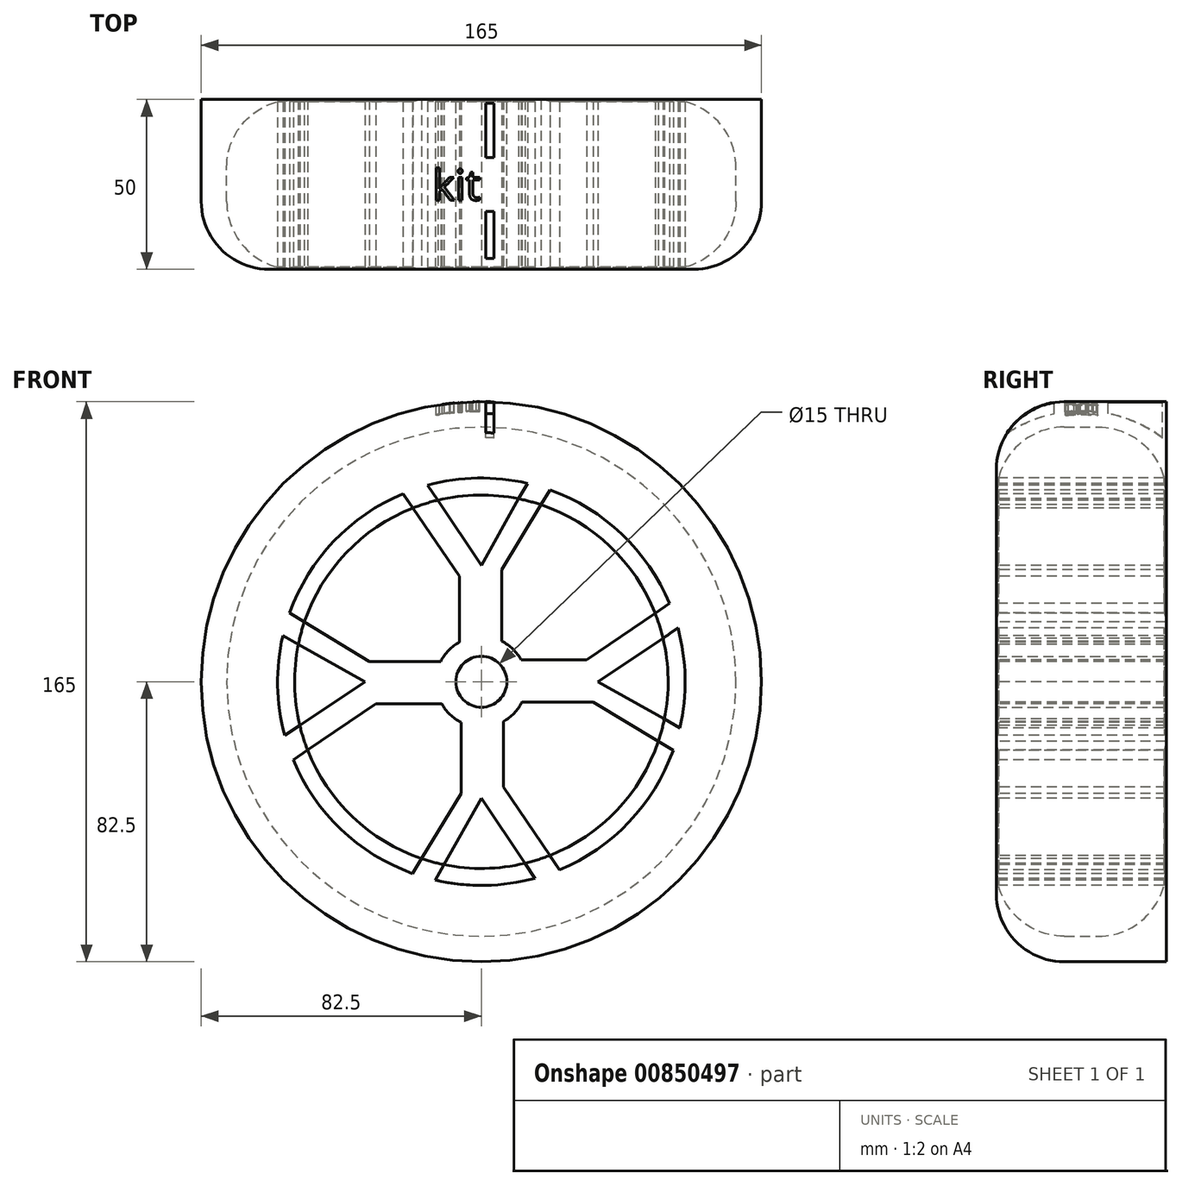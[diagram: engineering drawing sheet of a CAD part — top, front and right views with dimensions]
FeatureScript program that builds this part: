
annotation { "Feature Type Name" : "Feature", "Feature Type Description" : "" }
export const myFeature = defineFeature(function(context is Context, id is Id, definition is map)
    precondition{}
    {
        {
            var Q0;
            Q0=qCreatedBy(makeId("Front.planeOp"),FACE);
            var sketch = newSketch(context, id + "F0", { "sketchPlane" : qUnion([Q0])});
            skCircle(sketch, "E0", {"center": v(0, 0) * mm, "radius": 75 * mm});
            skCircle(sketch, "E1", {"center": v(0, 0) * mm, "radius": 7.5 * mm});
            skSolve(sketch);
        }
        {
            var Q0;
            Q0=makeQuery(id+"F0.imprint","IMPRINT",FACE,{"disambiguationData":[TD([[makeQuery(id+"F0.imprint","IMPRINT",EDGE,{"derivedFrom":sQuery(id+"F0.wireOp",EDGE,"E0")}),1.0]])]});
            var Q1;
            Q1 = qSketchRegion(id + "F2", true);
            extrude(context, id + "F1", {"entities" : qUnion([Q0, Q1]), "depth" : 25 * mm, "offsetDistance" : 25 * mm});
        }
        {
            var Q0;
            Q0=makeQuery(id+"F1.opExtrude","CAP_FACE",FACE,{"disambiguationData":[OSD([sQuery(id+"F0.wireOp",EDGE,"E0")])],"isStart":false});
            var sketch = newSketch(context, id + "F2", { "sketchPlane" : qUnion([Q0])});
            skPoint(sketch, "E2.center", {"position": v(0, 0) * mm});
            skCircle(sketch, "E3", {"center": v(0, 0) * mm, "radius": 60 * mm});
            skLineSegment(sketch, "E4", {"start": v(-13.56, -58.45) * mm, "end": v(0, -34.29) * mm});
            skLineSegment(sketch, "E5", {"start": v(0, -34.29) * mm, "end": v(15.8, -57.88) * mm});
            skLineSegment(sketch, "E6", {"start": v(6.45, -43.93) * mm, "end": v(6.45, 0) * mm});
            skLineSegment(sketch, "E7", {"start": v(-5.99, -44.96) * mm, "end": v(-5.99, 0) * mm});
            skCircle(sketch, "E8", {"center": v(0, 0) * mm, "radius": 10.6 * mm});
            skLineSegment(sketch, "E9", {"start": v(-20.24, -56.48) * mm, "end": v(-5.99, -32.95) * mm});
            skLineSegment(sketch, "E10", {"start": v(6.45, -31.06) * mm, "end": v(23.04, -55.4) * mm});
            skLineSegment(sketch, "E11.1.0", {"start": v(56.48, -20.24) * mm, "end": v(32.95, -5.99) * mm});
            skLineSegment(sketch, "E11.1.1", {"start": v(58.45, -13.56) * mm, "end": v(34.29, 0) * mm});
            skLineSegment(sketch, "E11.1.2", {"start": v(44.96, -5.99) * mm, "end": v(0, -5.99) * mm});
            skLineSegment(sketch, "E11.1.3", {"start": v(43.93, 6.45) * mm, "end": v(0, 6.45) * mm});
            skLineSegment(sketch, "E11.1.4", {"start": v(31.06, 6.45) * mm, "end": v(55.4, 23.04) * mm});
            skLineSegment(sketch, "E11.1.5", {"start": v(34.29, 0) * mm, "end": v(57.88, 15.8) * mm});
            skLineSegment(sketch, "E11.2.0", {"start": v(20.24, 56.48) * mm, "end": v(5.99, 32.95) * mm});
            skLineSegment(sketch, "E11.2.1", {"start": v(13.56, 58.45) * mm, "end": v(0, 34.29) * mm});
            skLineSegment(sketch, "E11.2.2", {"start": v(5.99, 44.96) * mm, "end": v(5.99, 0) * mm});
            skLineSegment(sketch, "E11.2.3", {"start": v(-6.45, 43.93) * mm, "end": v(-6.45, 0) * mm});
            skLineSegment(sketch, "E11.2.4", {"start": v(-6.45, 31.06) * mm, "end": v(-23.04, 55.4) * mm});
            skLineSegment(sketch, "E11.2.5", {"start": v(0, 34.29) * mm, "end": v(-15.8, 57.88) * mm});
            skLineSegment(sketch, "E11.3.0", {"start": v(-56.48, 20.24) * mm, "end": v(-32.95, 5.99) * mm});
            skLineSegment(sketch, "E11.3.1", {"start": v(-58.45, 13.56) * mm, "end": v(-34.29, 0) * mm});
            skLineSegment(sketch, "E11.3.2", {"start": v(-44.96, 5.99) * mm, "end": v(0, 5.99) * mm});
            skLineSegment(sketch, "E11.3.3", {"start": v(-43.93, -6.45) * mm, "end": v(0, -6.45) * mm});
            skLineSegment(sketch, "E11.3.4", {"start": v(-31.06, -6.45) * mm, "end": v(-55.4, -23.04) * mm});
            skLineSegment(sketch, "E11.3.5", {"start": v(-34.29, 0) * mm, "end": v(-57.88, -15.8) * mm});
            skLineSegment(sketch, "E12", {"start": v(49.36, -34.12) * mm, "end": v(29.65, -13.58) * mm});
            skLineSegment(sketch, "E13", {"start": v(29.65, -13.58) * mm, "end": v(12.4, -9.8) * mm});
            skLineSegment(sketch, "E14", {"start": v(12.4, -9.8) * mm, "end": v(14.53, -27.76) * mm});
            skLineSegment(sketch, "E15", {"start": v(14.53, -27.76) * mm, "end": v(35.64, -48.26) * mm});
            skLineSegment(sketch, "E16.1.0", {"start": v(34.12, 49.36) * mm, "end": v(13.58, 29.65) * mm});
            skLineSegment(sketch, "E16.1.1", {"start": v(13.58, 29.65) * mm, "end": v(9.8, 12.4) * mm});
            skLineSegment(sketch, "E16.1.2", {"start": v(9.8, 12.4) * mm, "end": v(27.76, 14.53) * mm});
            skLineSegment(sketch, "E16.1.3", {"start": v(27.76, 14.53) * mm, "end": v(48.26, 35.64) * mm});
            skLineSegment(sketch, "E16.2.0", {"start": v(-49.36, 34.12) * mm, "end": v(-29.65, 13.58) * mm});
            skLineSegment(sketch, "E16.2.1", {"start": v(-29.65, 13.58) * mm, "end": v(-12.4, 9.8) * mm});
            skLineSegment(sketch, "E16.2.2", {"start": v(-12.4, 9.8) * mm, "end": v(-14.53, 27.76) * mm});
            skLineSegment(sketch, "E16.2.3", {"start": v(-14.53, 27.76) * mm, "end": v(-35.64, 48.26) * mm});
            skLineSegment(sketch, "E16.3.0", {"start": v(-34.12, -49.36) * mm, "end": v(-13.58, -29.65) * mm});
            skLineSegment(sketch, "E16.3.1", {"start": v(-13.58, -29.65) * mm, "end": v(-9.8, -12.4) * mm});
            skLineSegment(sketch, "E16.3.2", {"start": v(-9.8, -12.4) * mm, "end": v(-27.76, -14.53) * mm});
            skLineSegment(sketch, "E16.3.3", {"start": v(-27.76, -14.53) * mm, "end": v(-48.26, -35.64) * mm});
            skCircle(sketch, "E17", {"center": v(0, 0) * mm, "radius": 13.37 * mm});
            skSolve(sketch);
        }
        {
            var Q0;
            Q0=makeQuery(id+"F1.opExtrude","CAP_EDGE",EDGE,{"disambiguationData":[OSD([sQuery(id+"F0.wireOp",EDGE,"E0")])],"isStart":false});
            fillet(context, id + "F3", {"entities" : qUnion([Q0]), "radius" : 20 * mm, "tangentPropagation" : true, "allowEdgeOverflow" : false});
        }
        {
            var Q0;
            Q0=makeQuery(id+"F1.opExtrude","SWEPT_BODY",BODY,{"disambiguationData":[OSD([sQuery(id+"F0.wireOp",EDGE,"E0")])]});
            var Q1;
            Q1=makeQuery(id+"F1.opExtrude","CAP_FACE",FACE,{"disambiguationData":[OSD([sQuery(id+"F0.wireOp",EDGE,"E0")])],"isStart":true});
            mirror(context, id + "F4", {"operationType" : NewBodyOperationType.ADD, "entities" : qUnion([Q0]), "mirrorPlane" : qUnion([Q1])});
        }
        {
            var Q0;
            Q0=makeQuery(id+"F1.opExtrude","CAP_FACE",FACE,{"disambiguationData":[OSD([sQuery(id+"F0.wireOp",EDGE,"E0"),sQuery(id+"F0.wireOp",EDGE,"E1")])],"isStart":false});
            var sketch = newSketch(context, id + "F5", { "sketchPlane" : qUnion([Q0])});
            skCircle(sketch, "E18", {"center": v(0, 0) * mm, "radius": 82.5 * mm});
            skCircle(sketch, "E19", {"center": v(0, 0) * mm, "radius": 75 * mm});
            skSolve(sketch);
        }
        {
            var Q0;
            Q0=makeQuery(id+"F5.imprint","IMPRINT",FACE,{"disambiguationData":[TD([[makeQuery(id+"F5.imprint","IMPRINT",EDGE,{"derivedFrom":sQuery(id+"F5.wireOp",EDGE,"E18")}),1.0]])]});
            var Q1;
            Q1=makeQuery(id+"F5.imprint","IMPRINT",FACE,{"disambiguationData":[TD([[makeQuery(id+"F5.imprint","IMPRINT",EDGE,{"derivedFrom":sQuery(id+"F5.wireOp",EDGE,"E19")}),1.0]])]});
            var Q2;
            Q2=makeQuery(id+"F4.opPattern","COPY",FACE,{"derivedFrom":makeQuery(id+"F1.opExtrude","CAP_FACE",FACE,{"disambiguationData":[OSD([sQuery(id+"F0.wireOp",EDGE,"E0"),sQuery(id+"F0.wireOp",EDGE,"E1")])],"isStart":false}),"instanceName":"1"});
            extrude(context, id + "F6", {"entities" : qUnion([Q0, Q1]), "endBound" : BoundingType.UP_TO_SURFACE, "oppositeDirection" : true, "depth" : 25 * mm, "endBoundEntityFace" : qUnion([Q2]), "offsetDistance" : 25 * mm});
        }
        {
            var Q0;
            Q0=makeQuery(id+"F6.opExtrude","CAP_EDGE",EDGE,{"disambiguationData":[OSD([sQuery(id+"F5.wireOp",EDGE,"E18")])],"isStart":true});
            var Q1;
            Q1=makeQuery(id+"F6.opExtrude","TWEAK_EDGE",EDGE,{"derivedFrom":[makeQuery(id+"F4.opPattern","COPY",FACE,{"derivedFrom":makeQuery(id+"F1.opExtrude","CAP_FACE",FACE,{"disambiguationData":[OSD([sQuery(id+"F0.wireOp",EDGE,"E0"),sQuery(id+"F0.wireOp",EDGE,"E1")])],"isStart":false}),"instanceName":"1"}),makeQuery(id+"F5.imprint","IMPRINT",EDGE,{"derivedFrom":sQuery(id+"F5.wireOp",EDGE,"E18")})]});
            fillet(context, id + "F7", {"entities" : qUnion([Q0, Q1]), "radius" : 20 * mm, "tangentPropagation" : true, "allowEdgeOverflow" : false});
        }
        {
            var Q0;
            Q0=qCreatedBy(makeId("Right.planeOp"),FACE);
            var sketch = newSketch(context, id + "F8", { "sketchPlane" : qUnion([Q0])});
            skArc(sketch, "E20", {"start": v(26.8, 69.52) * mm, "mid": v(1.15, 79.8) * mm, "end": v(-25.05, 71) * mm});
            skSolve(sketch);
        }
        {
            var Q0;
            Q0=sQuery(id+"F8.wireOp",EDGE,"E20");
            var Q1;
            Q1=sQuery(id+"F0.wireOp",EDGE,"E1");
            revolve(context, id + "F9", {"bodyType" : ToolBodyType.SURFACE, "surfaceOperationType" : NewSurfaceOperationType.NEW, "surfaceEntities" : qUnion([Q0]), "axis" : qUnion([Q1]), "revolveType" : RevolveType.FULL});
        }
        {
            var Q0;
            {var subQ1=sQuery(id+"F2.wireOp",EDGE,"E10");Q0=makeQuery(id+"F2.imprint","IMPRINT",FACE,{"disambiguationData":[TD([[makeQuery(id+"F2.imprint","IMPRINT",EDGE,{"derivedFrom":subQ1}),1.0]])]});}
            var Q1;
            {var subQ7=sQuery(id+"F2.wireOp",EDGE,"E11.1.4");Q1=makeQuery(id+"F2.imprint","IMPRINT",FACE,{"disambiguationData":[TD([[makeQuery(id+"F2.imprint","IMPRINT",EDGE,{"derivedFrom":subQ7}),1.0]])]});}
            var Q2;
            {var subQ0=sQuery(id+"F2.wireOp",EDGE,"E16.1.0");Q2=makeQuery(id+"F2.imprint","IMPRINT",FACE,{"disambiguationData":[TD([[makeQuery(id+"F2.imprint","IMPRINT",EDGE,{"derivedFrom":subQ0}),1.0]])]});}
            var Q3;
            {var subQ0=sQuery(id+"F2.wireOp",EDGE,"E12");Q3=makeQuery(id+"F2.imprint","IMPRINT",FACE,{"disambiguationData":[TD([[makeQuery(id+"F2.imprint","IMPRINT",EDGE,{"derivedFrom":subQ0}),1.0]])]});}
            var Q4;
            {var subQ0=sQuery(id+"F2.wireOp",EDGE,"E11.1.1");var subQ1=sQuery(id+"F2.wireOp",EDGE,"E3");var subQ2=makeQuery(id+"F2.imprint","INTERSECT",VERTEX,{"derivedFrom":[subQ1,subQ0]});Q4=makeQuery(id+"F2.imprint","IMPRINT",FACE,{"disambiguationData":[TD([[makeQuery(id+"F2.imprint","IMPRINT",EDGE,{"disambiguationData":[TD([[subQ2,-1.0]])],"derivedFrom":subQ1}),1.0]])]});}
            var Q5;
            {var subQ1=sQuery(id+"F2.wireOp",EDGE,"E11.2.1");var subQ4=sQuery(id+"F2.wireOp",EDGE,"E3");var subQ5=makeQuery(id+"F2.imprint","INTERSECT",VERTEX,{"derivedFrom":[subQ4,subQ1]});Q5=makeQuery(id+"F2.imprint","IMPRINT",FACE,{"disambiguationData":[TD([[makeQuery(id+"F2.imprint","IMPRINT",EDGE,{"disambiguationData":[TD([[subQ5,-1.0]])],"derivedFrom":subQ4}),1.0]])]});}
            var Q6;
            {var subQ0=sQuery(id+"F2.wireOp",EDGE,"E16.2.0");Q6=makeQuery(id+"F2.imprint","IMPRINT",FACE,{"disambiguationData":[TD([[makeQuery(id+"F2.imprint","IMPRINT",EDGE,{"derivedFrom":subQ0}),1.0]])]});}
            var Q7;
            {var subQ1=sQuery(id+"F2.wireOp",EDGE,"E11.2.4");Q7=makeQuery(id+"F2.imprint","IMPRINT",FACE,{"disambiguationData":[TD([[makeQuery(id+"F2.imprint","IMPRINT",EDGE,{"derivedFrom":subQ1}),1.0]])]});}
            var Q8;
            {var subQ0=sQuery(id+"F2.wireOp",EDGE,"E11.3.1");var subQ1=sQuery(id+"F2.wireOp",EDGE,"E3");var subQ2=makeQuery(id+"F2.imprint","INTERSECT",VERTEX,{"derivedFrom":[subQ1,subQ0]});Q8=makeQuery(id+"F2.imprint","IMPRINT",FACE,{"disambiguationData":[TD([[makeQuery(id+"F2.imprint","IMPRINT",EDGE,{"disambiguationData":[TD([[subQ2,-1.0]])],"derivedFrom":subQ1}),1.0]])]});}
            var Q9;
            {var subQ0=sQuery(id+"F2.wireOp",EDGE,"E16.3.0");Q9=makeQuery(id+"F2.imprint","IMPRINT",FACE,{"disambiguationData":[TD([[makeQuery(id+"F2.imprint","IMPRINT",EDGE,{"derivedFrom":subQ0}),1.0]])]});}
            var Q10;
            {var subQ0=sQuery(id+"F2.wireOp",EDGE,"E9");Q10=makeQuery(id+"F2.imprint","IMPRINT",FACE,{"disambiguationData":[TD([[makeQuery(id+"F2.imprint","IMPRINT",EDGE,{"derivedFrom":subQ0}),1.0]])]});}
            var Q11;
            {var subQ1=sQuery(id+"F2.wireOp",EDGE,"E4");var subQ5=sQuery(id+"F2.wireOp",EDGE,"E3");var subQ6=makeQuery(id+"F2.imprint","INTERSECT",VERTEX,{"derivedFrom":[subQ5,subQ1]});Q11=makeQuery(id+"F2.imprint","IMPRINT",FACE,{"disambiguationData":[TD([[makeQuery(id+"F2.imprint","IMPRINT",EDGE,{"disambiguationData":[TD([[subQ6,-1.0]])],"derivedFrom":subQ5}),1.0]])]});}
            extrude(context, id + "F10", {"entities" : qUnion([Q0, Q1, Q2, Q3, Q4, Q5, Q6, Q7, Q8, Q9, Q10, Q11]), "operationType" : NewBodyOperationType.REMOVE, "endBound" : BoundingType.UP_TO_NEXT, "oppositeDirection" : true, "depth" : 50 * mm, "offsetDistance" : 25 * mm});
        }
        {
            var Q0;
            Q0=qCreatedBy(makeId("Top.planeOp"),FACE);
            cPlane(context, id + "F11", {"entities" : qUnion([Q0]), "cplaneType" : CPlaneType.OFFSET, "offset" : 82.5 * mm, "width" : 150 * mm, "height" : 150 * mm});
        }
        {
            var Q0;
            Q0 = qConstructionFilter(qBodyType(qCreatedBy(id + "F8" ,EDGE), BodyType.WIRE), ConstructionObject.NO);
            var Q1;
            Q1=makeQuery(id+"F6.opExtrude","SWEPT_FACE",FACE,{"disambiguationData":[OSD([sQuery(id+"F5.wireOp",EDGE,"E18")])]});
            revolve(context, id + "F12", {"bodyType" : ToolBodyType.SURFACE, "surfaceOperationType" : NewSurfaceOperationType.NEW, "surfaceEntities" : qUnion([Q0]), "axis" : qUnion([Q1]), "revolveType" : RevolveType.FULL});
        }
        {
            var Q0;
            Q0=qCreatedBy(id+"F11.planeOp",FACE);
            var sketch = newSketch(context, id + "F13", { "sketchPlane" : qUnion([Q0])});
            skLineSegment(sketch, "E21.bottom", {"start": v(1.23, -23.92) * mm, "end": v(3.73, -23.92) * mm});
            skLineSegment(sketch, "E21.top", {"start": v(1.23, -7.92) * mm, "end": v(3.73, -7.92) * mm});
            skLineSegment(sketch, "E21.left", {"start": v(1.23, -23.92) * mm, "end": v(1.23, -7.92) * mm});
            skLineSegment(sketch, "E21.right", {"start": v(3.73, -23.92) * mm, "end": v(3.73, -7.92) * mm});
            skLineSegment(sketch, "E22.MirrorCS", {"start": v(1.23, 23.92) * mm, "end": v(1.23, 7.92) * mm});
            skLineSegment(sketch, "E23.MirrorCS", {"start": v(3.73, 23.92) * mm, "end": v(3.73, 7.92) * mm});
            skLineSegment(sketch, "E24.MirrorCS", {"start": v(1.23, 7.92) * mm, "end": v(3.73, 7.92) * mm});
            skLineSegment(sketch, "E25.MirrorCS", {"start": v(1.23, 23.92) * mm, "end": v(3.73, 23.92) * mm});
            skSolve(sketch);
        }
        {
            var Q0;
            Q0 = qSketchRegion(id + "F13", true);
            var Q1;
            Q1=makeQuery(id+"F9.opRevolve","SWEPT_FACE",FACE,{"disambiguationData":[OSD([sQuery(id+"F8.wireOp",EDGE,"E20")])]});
            extrude(context, id + "F14", {"entities" : qUnion([Q0]), "operationType" : NewBodyOperationType.REMOVE, "endBound" : BoundingType.UP_TO_SURFACE, "oppositeDirection" : true, "depth" : 25 * mm, "endBoundEntityFace" : qUnion([Q1]), "offsetDistance" : 25 * mm});
        }
        {
            var Q0;
            Q0=qCreatedBy(makeId("Top.planeOp"),FACE);
            cPlane(context, id + "F15", {"entities" : qUnion([Q0]), "cplaneType" : CPlaneType.OFFSET, "offset" : 100 * mm, "width" : 150 * mm, "height" : 150 * mm});
        }
        {
            var Q0;
            Q0=qCreatedBy(id+"F15.planeOp",FACE);
            var sketch = newSketch(context, id + "F16", { "sketchPlane" : qUnion([Q0])});
            skText(sketch, "E26", { "text": "kit", "fontName": "OpenSans-Regular.ttf"});
            const initialGuessF16  = {"E26": [-0.0144, -0.00463, 1, 0, 0.00903]};
            skSetInitialGuess(sketch, initialGuessF16);
            skSolve(sketch);
        }
        {
            var Q0;
            Q0 = qSketchRegion(id + "F16", true);
            var Q1;
            Q1=makeQuery(id+"F9.opRevolve","SWEPT_FACE",FACE,{"disambiguationData":[OSD([sQuery(id+"F8.wireOp",EDGE,"E20")])]});
            extrude(context, id + "F17", {"entities" : qUnion([Q0]), "operationType" : NewBodyOperationType.REMOVE, "endBound" : BoundingType.UP_TO_SURFACE, "oppositeDirection" : true, "depth" : 25 * mm, "endBoundEntityFace" : qUnion([Q1]), "offsetDistance" : 25 * mm});
        }
    });
